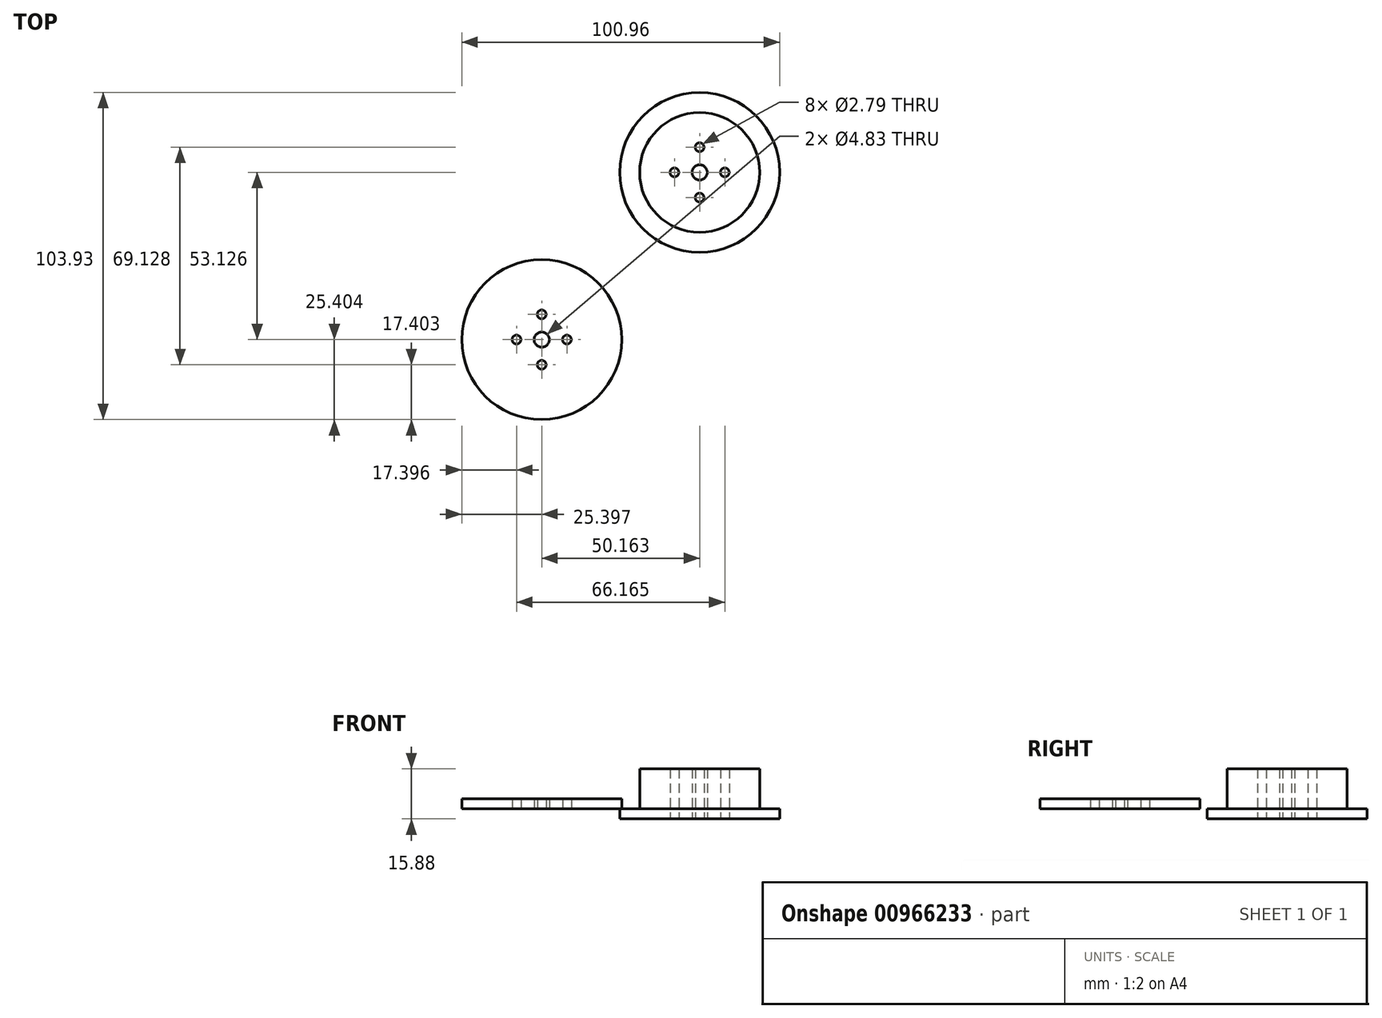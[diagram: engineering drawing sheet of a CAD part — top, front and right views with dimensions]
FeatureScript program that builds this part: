
annotation { "Feature Type Name" : "Feature", "Feature Type Description" : "" }
export const myFeature = defineFeature(function(context is Context, id is Id, definition is map)
    precondition{}
    {
        {
            var Q0;
            Q0=qCreatedBy(makeId("Top.planeOp"),FACE);
            var sketch = newSketch(context, id + "F0", { "sketchPlane" : qUnion([Q0])});
            skCircle(sketch, "E0", {"center": v(0, 0) * mm, "radius": 25.4 * mm});
            skCircle(sketch, "E1", {"center": v(0, 0) * mm, "radius": 19.05 * mm});
            skCircle(sketch, "E2", {"center": v(0, 0) * mm, "radius": 2.41 * mm});
            skCircle(sketch, "E3", {"center": v(0, 8) * mm, "radius": 1.4 * mm});
            skCircle(sketch, "E4", {"center": v(-8, 0) * mm, "radius": 1.4 * mm});
            skCircle(sketch, "E5", {"center": v(8, 0) * mm, "radius": 1.4 * mm});
            skCircle(sketch, "E6", {"center": v(0, -8) * mm, "radius": 1.4 * mm});
            skSolve(sketch);
        }
        {
            var Q0;
            Q0=makeQuery(id+"F0.imprint","IMPRINT",FACE,{"disambiguationData":[TD([[makeQuery(id+"F0.imprint","IMPRINT",EDGE,{"derivedFrom":sQuery(id+"F0.wireOp",EDGE,"E1")}),1.0]])]});
            extrude(context, id + "F1", {"entities" : qUnion([Q0]), "depth" : 12.7 * mm});
        }
        {
            var Q0;
            Q0=makeQuery(id+"F0.imprint","IMPRINT",FACE,{"disambiguationData":[TD([[makeQuery(id+"F0.imprint","IMPRINT",EDGE,{"derivedFrom":sQuery(id+"F0.wireOp",EDGE,"E0")}),1.0]])]});
            var Q1;
            Q1=makeQuery(id+"F0.imprint","IMPRINT",FACE,{"disambiguationData":[TD([[makeQuery(id+"F0.imprint","IMPRINT",EDGE,{"derivedFrom":sQuery(id+"F0.wireOp",EDGE,"E1")}),1.0]])]});
            extrude(context, id + "F2", {"entities" : qUnion([Q0, Q1]), "operationType" : NewBodyOperationType.ADD, "oppositeDirection" : true, "depth" : 3.17 * mm});
        }
        {
            var Q0;
            Q0=qCreatedBy(makeId("Top.planeOp"),FACE);
            var sketch = newSketch(context, id + "F3", { "sketchPlane" : qUnion([Q0])});
            skCircle(sketch, "E7", {"center": v(-50.16, -53.13) * mm, "radius": 25.4 * mm});
            skCircle(sketch, "E8", {"center": v(-50.16, -53.13) * mm, "radius": 19.05 * mm});
            skCircle(sketch, "E9", {"center": v(-50.16, -53.13) * mm, "radius": 2.41 * mm});
            skCircle(sketch, "E10", {"center": v(-50.16, -45.13) * mm, "radius": 1.4 * mm});
            skCircle(sketch, "E11", {"center": v(-58.16, -53.13) * mm, "radius": 1.4 * mm});
            skCircle(sketch, "E12", {"center": v(-42.16, -53.13) * mm, "radius": 1.4 * mm});
            skCircle(sketch, "E13", {"center": v(-50.16, -61.13) * mm, "radius": 1.4 * mm});
            skSolve(sketch);
        }
        {
            var Q0;
            Q0=makeQuery(id+"F3.imprint","IMPRINT",FACE,{"disambiguationData":[TD([[makeQuery(id+"F3.imprint","IMPRINT",EDGE,{"derivedFrom":sQuery(id+"F3.wireOp",EDGE,"E8")}),1.0]])]});
            var Q1;
            Q1=makeQuery(id+"F3.imprint","IMPRINT",FACE,{"disambiguationData":[TD([[makeQuery(id+"F3.imprint","IMPRINT",EDGE,{"derivedFrom":sQuery(id+"F3.wireOp",EDGE,"E7")}),1.0]])]});
            extrude(context, id + "F4", {"entities" : qUnion([Q0, Q1]), "depth" : 3.17 * mm});
        }
    });
